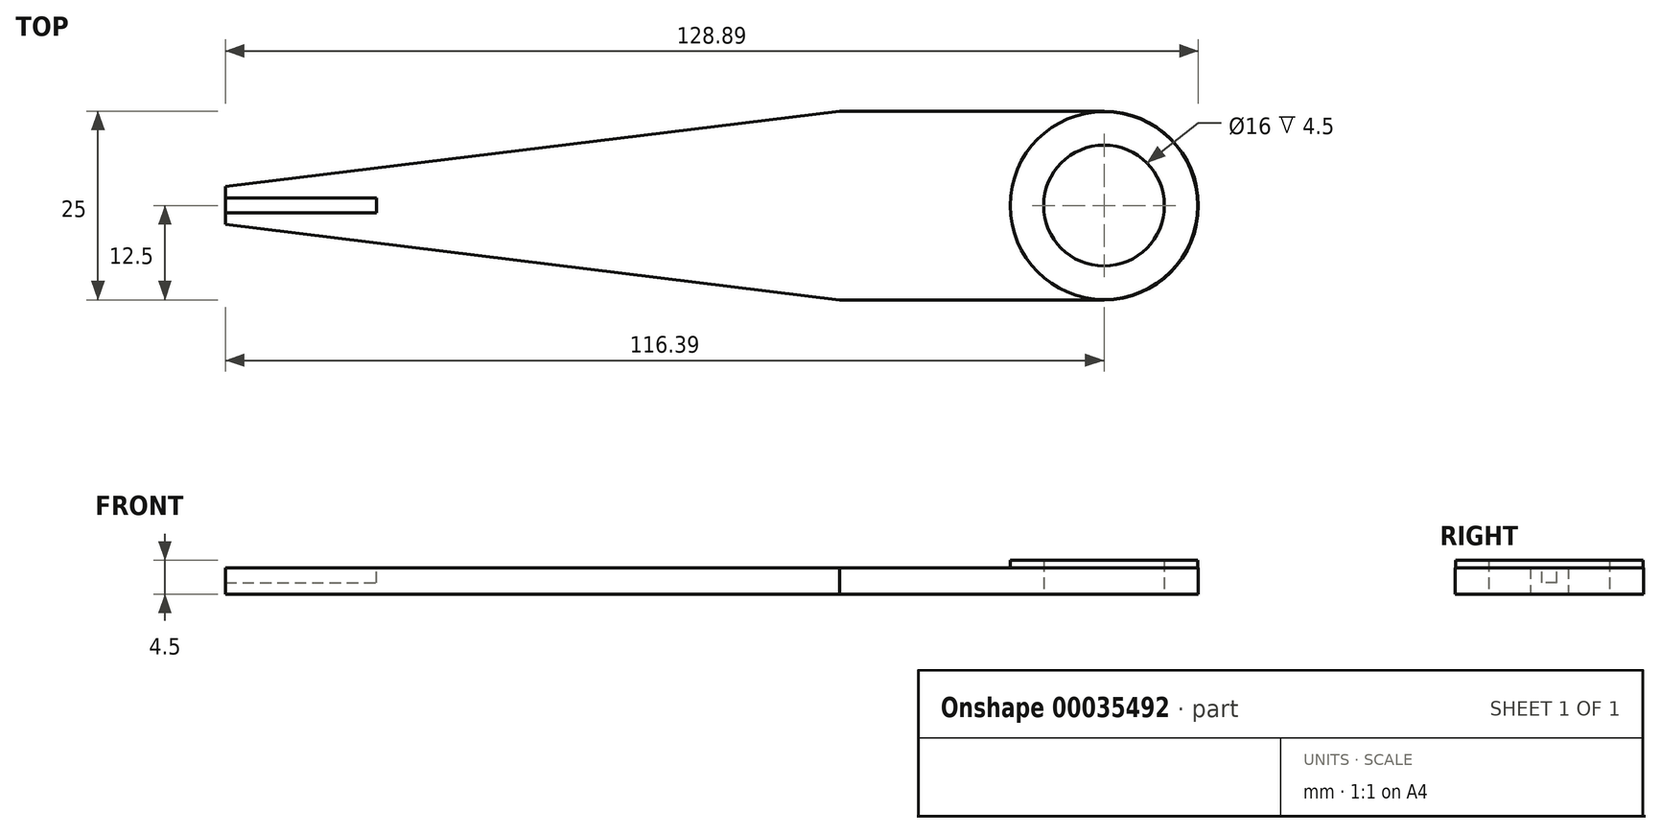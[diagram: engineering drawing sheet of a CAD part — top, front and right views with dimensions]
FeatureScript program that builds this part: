
annotation { "Feature Type Name" : "Feature", "Feature Type Description" : "" }
export const myFeature = defineFeature(function(context is Context, id is Id, definition is map)
    precondition{}
    {
        {
            var Q0;
            Q0=qCreatedBy(makeId("Top.planeOp"),FACE);
            var sketch = newSketch(context, id + "F0", { "sketchPlane" : qUnion([Q0])});
            skCircle(sketch, "E0", {"center": v(0, 0) * mm, "radius": 8 * mm});
            skCircle(sketch, "E1", {"center": v(0, 0) * mm, "radius": 12.5 * mm});
            skLineSegment(sketch, "E2", {"start": v(-35, 12.5) * mm, "end": v(0, 12.5) * mm});
            skLineSegment(sketch, "E3", {"start": v(-35, -12.5) * mm, "end": v(0, -12.5) * mm});
            skLineSegment(sketch, "E4", {"start": v(-35, 12.5) * mm, "end": v(-78.5, 12.5) * mm, "construction": true});
            skLineSegment(sketch, "E5", {"start": v(-35, 12.5) * mm, "end": v(-116.39, 2.5) * mm});
            skLineSegment(sketch, "E6", {"start": v(-35, -12.5) * mm, "end": v(-78.28, -12.5) * mm, "construction": true});
            skLineSegment(sketch, "E7", {"start": v(-35, -12.5) * mm, "end": v(-116.39, -2.5) * mm});
            skLineSegment(sketch, "E8", {"start": v(-116.39, 2.5) * mm, "end": v(-116.39, -2.5) * mm});
            skSolve(sketch);
        }
        {
            var Q0;
            Q0 = qSketchRegion(id + "F0", true);
            extrude(context, id + "F1", {"entities" : qUnion([Q0]), "depth" : 3.5 * mm});
        }
        {
            var Q0;
            Q0=makeQuery(id+"F1.opExtrude","CAP_FACE",FACE,{"disambiguationData":[OSD([sQuery(id+"F0.wireOp",EDGE,"E0"),sQuery(id+"F0.wireOp",EDGE,"E1"),sQuery(id+"F0.wireOp",EDGE,"E2"),sQuery(id+"F0.wireOp",EDGE,"E3"),sQuery(id+"F0.wireOp",EDGE,"E5"),sQuery(id+"F0.wireOp",EDGE,"E7"),sQuery(id+"F0.wireOp",EDGE,"E8")])],"isStart":false});
            var sketch = newSketch(context, id + "F2", { "sketchPlane" : qUnion([Q0])});
            skCircle(sketch, "E9", {"center": v(0, 0) * mm, "radius": 12.43 * mm});
            skCircle(sketch, "E10", {"center": v(0, 0) * mm, "radius": 8 * mm});
            skSolve(sketch);
        }
        {
            var Q0;
            Q0 = qSketchRegion(id + "F2", true);
            extrude(context, id + "F3", {"entities" : qUnion([Q0]), "operationType" : NewBodyOperationType.ADD, "depth" : 1 * mm});
        }
        {
            var Q0;
            Q0=makeQuery(id+"F1.opExtrude","CAP_FACE",FACE,{"disambiguationData":[OSD([sQuery(id+"F0.wireOp",EDGE,"E0"),sQuery(id+"F0.wireOp",EDGE,"E1"),sQuery(id+"F0.wireOp",EDGE,"E2"),sQuery(id+"F0.wireOp",EDGE,"E3"),sQuery(id+"F0.wireOp",EDGE,"E5"),sQuery(id+"F0.wireOp",EDGE,"E7"),sQuery(id+"F0.wireOp",EDGE,"E8")])],"isStart":false});
            var sketch = newSketch(context, id + "F4", { "sketchPlane" : qUnion([Q0])});
            skLineSegment(sketch, "E11.bottom", {"start": v(-116.39, 1) * mm, "end": v(-96.39, 1) * mm});
            skLineSegment(sketch, "E11.top", {"start": v(-116.39, -1) * mm, "end": v(-96.39, -1) * mm});
            skLineSegment(sketch, "E11.left", {"start": v(-116.39, 1) * mm, "end": v(-116.39, -1) * mm});
            skLineSegment(sketch, "E11.right", {"start": v(-96.39, 1) * mm, "end": v(-96.39, -1) * mm});
            skSolve(sketch);
        }
        {
            var Q0;
            Q0 = qSketchRegion(id + "F4", true);
            extrude(context, id + "F5", {"entities" : qUnion([Q0]), "operationType" : NewBodyOperationType.REMOVE, "oppositeDirection" : true, "depth" : 2 * mm});
        }
    });
